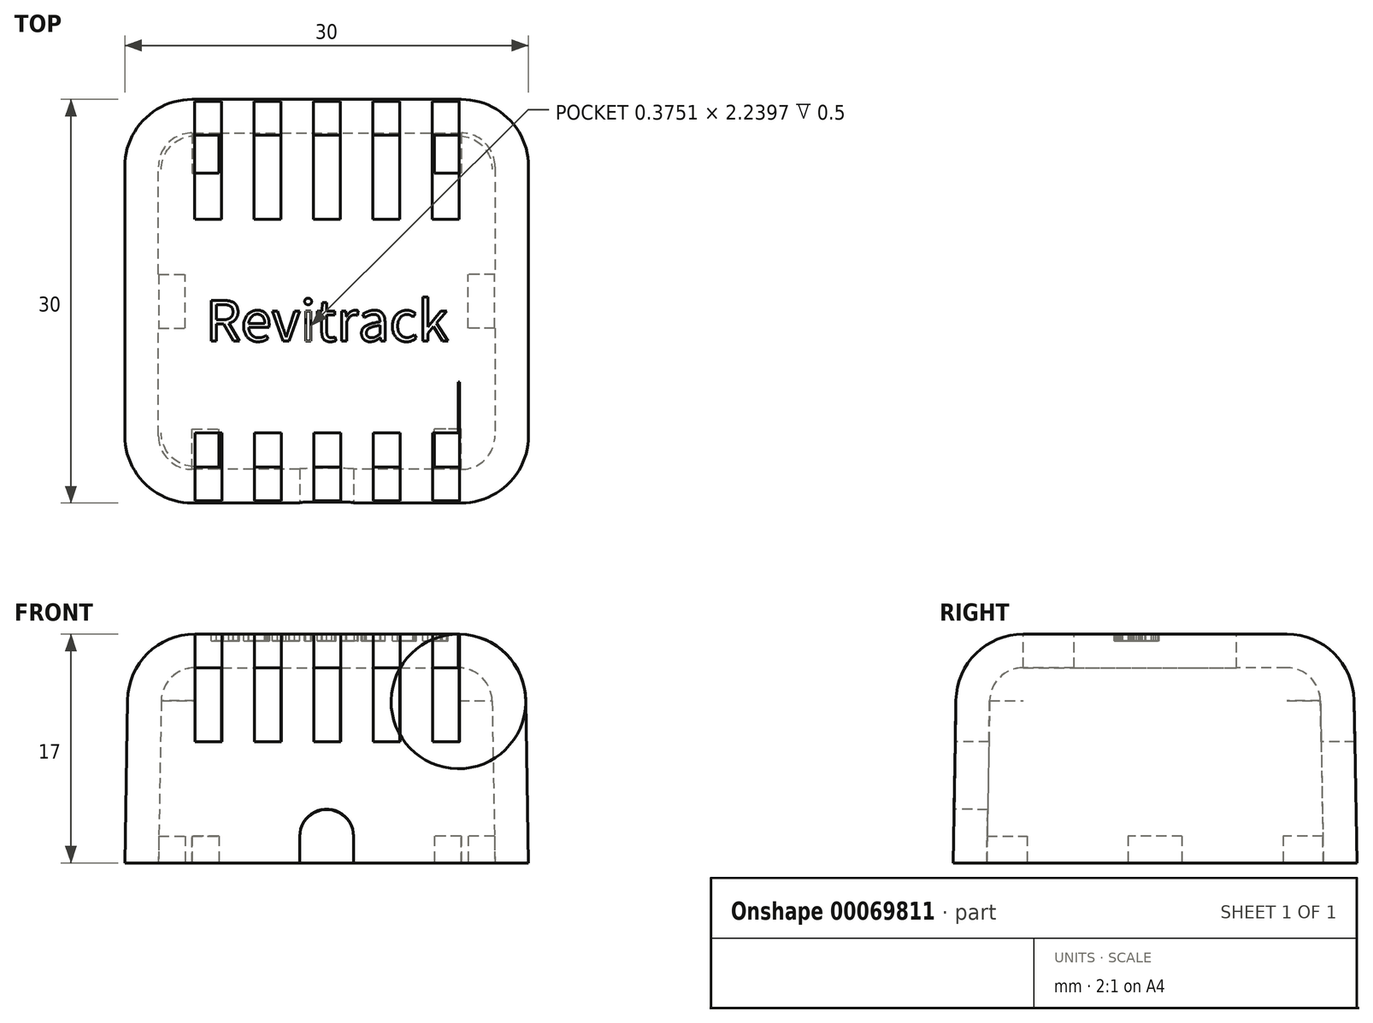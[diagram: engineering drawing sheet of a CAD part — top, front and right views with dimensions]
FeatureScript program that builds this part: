
annotation { "Feature Type Name" : "Feature", "Feature Type Description" : "" }
export const myFeature = defineFeature(function(context is Context, id is Id, definition is map)
    precondition{}
    {
        {
            var Q0;
            Q0=qCreatedBy(makeId("Top.planeOp"),FACE);
            var sketch = newSketch(context, id + "F0", { "sketchPlane" : qUnion([Q0])});
            skLineSegment(sketch, "E0.rect.bottom", {"start": v(15, 15) * mm, "end": v(-15, 15) * mm});
            skLineSegment(sketch, "E0.rect.top", {"start": v(15, -15) * mm, "end": v(-15, -15) * mm});
            skLineSegment(sketch, "E0.rect.left", {"start": v(15, 15) * mm, "end": v(15, -15) * mm});
            skLineSegment(sketch, "E0.rect.right", {"start": v(-15, 15) * mm, "end": v(-15, -15) * mm});
            skPoint(sketch, "E0.rect.middle", {"position": v(0, 0) * mm});
            skSolve(sketch);
        }
        {
            var Q0;
            Q0=makeQuery(id+"F0.imprint","IMPRINT",FACE,{"disambiguationData":[TD([[makeQuery(id+"F0.imprint","IMPRINT",EDGE,{"derivedFrom":sQuery(id+"F0.wireOp",EDGE,"E0.rect.bottom")}),1.0]])]});
            extrude(context, id + "F1", {"entities" : qUnion([Q0]), "depth" : 17 * mm, "hasDraft" : true, "draftAngle" : 1 * degree, "draftPullDirection" : true});
        }
        {
            var Q0;
            Q0=makeQuery(id+"F1.opExtrude","CAP_FACE",FACE,{"disambiguationData":[OSD([sQuery(id+"F0.wireOp",EDGE,"E0.rect.bottom"),sQuery(id+"F0.wireOp",EDGE,"E0.rect.top"),sQuery(id+"F0.wireOp",EDGE,"E0.rect.left"),sQuery(id+"F0.wireOp",EDGE,"E0.rect.right")])],"isStart":false});
            var Q1;
            Q1=makeQuery(id+"F1.opExtrude","SWEPT_EDGE",EDGE,{"disambiguationData":[OSD([sQuery(id+"F0.wireOp",EDGE,"E0.rect.bottom"),sQuery(id+"F0.wireOp",EDGE,"E0.rect.left")])]});
            var Q2;
            Q2=makeQuery(id+"F1.opExtrude","SWEPT_EDGE",EDGE,{"disambiguationData":[OSD([sQuery(id+"F0.wireOp",EDGE,"E0.rect.top"),sQuery(id+"F0.wireOp",EDGE,"E0.rect.left")])]});
            var Q3;
            Q3=makeQuery(id+"F1.opExtrude","SWEPT_EDGE",EDGE,{"disambiguationData":[OSD([sQuery(id+"F0.wireOp",EDGE,"E0.rect.top"),sQuery(id+"F0.wireOp",EDGE,"E0.rect.right")])]});
            var Q4;
            Q4=makeQuery(id+"F1.opExtrude","SWEPT_EDGE",EDGE,{"disambiguationData":[OSD([sQuery(id+"F0.wireOp",EDGE,"E0.rect.bottom"),sQuery(id+"F0.wireOp",EDGE,"E0.rect.right")])]});
            fillet(context, id + "F2", {"entities" : qUnion([Q0, Q1, Q2, Q3, Q4]), "radius" : 5 * mm, "tangentPropagation" : true, "allowEdgeOverflow" : false});
        }
        {
            var Q0;
            Q0=makeQuery(id+"F1.opExtrude","CAP_FACE",FACE,{"disambiguationData":[OSD([sQuery(id+"F0.wireOp",EDGE,"E0.rect.bottom"),sQuery(id+"F0.wireOp",EDGE,"E0.rect.top"),sQuery(id+"F0.wireOp",EDGE,"E0.rect.left"),sQuery(id+"F0.wireOp",EDGE,"E0.rect.right")])],"isStart":true});
            shell(context, id + "F3", {"entities" : qUnion([Q0]), "thickness" : 2.5 * mm});
        }
        {
            var Q0;
            Q0=makeQuery(id+"F1.opExtrude","CAP_FACE",FACE,{"disambiguationData":[OSD([sQuery(id+"F0.wireOp",EDGE,"E0.rect.bottom"),sQuery(id+"F0.wireOp",EDGE,"E0.rect.top"),sQuery(id+"F0.wireOp",EDGE,"E0.rect.left"),sQuery(id+"F0.wireOp",EDGE,"E0.rect.right")])],"isStart":false});
            var sketch = newSketch(context, id + "F4", { "sketchPlane" : qUnion([Q0])});
            skLineSegment(sketch, "E1", {"start": v(0, 9.79) * mm, "end": v(0, -9.79) * mm, "construction": true});
            skLineSegment(sketch, "E2", {"start": v(-9.79, 6) * mm, "end": v(9.79, 6) * mm});
            skLineSegment(sketch, "E3", {"start": v(-9.79, -6) * mm, "end": v(9.79, -6) * mm});
            skLineSegment(sketch, "E4", {"start": v(-9.79, 0) * mm, "end": v(9.79, 0) * mm, "construction": true});
            skLineSegment(sketch, "E5.0", {"start": v(10, -15) * mm, "end": v(-10, -15) * mm, "construction": true});
            skEllipticalArc(sketch, "E5.1", {"construction": true});
            skEllipticalArc(sketch, "E6.0", {"construction": true});
            skLineSegment(sketch, "E7.0", {"start": v(15, 10) * mm, "end": v(15, -10) * mm, "construction": true});
            skEllipticalArc(sketch, "E8.0", {"construction": true});
            skLineSegment(sketch, "E9.0", {"start": v(10, 15) * mm, "end": v(-10, 15) * mm, "construction": true});
            skEllipticalArc(sketch, "E10.0", {"construction": true});
            skLineSegment(sketch, "E11.0", {"start": v(-15, 10) * mm, "end": v(-15, -10) * mm, "construction": true});
            skLineSegment(sketch, "E12.bottom", {"start": v(-9.79, -6) * mm, "end": v(-7.79, -6) * mm});
            skLineSegment(sketch, "E12.top", {"start": v(-9.79, -15) * mm, "end": v(-7.79, -15) * mm});
            skLineSegment(sketch, "E12.left", {"start": v(-9.79, -6) * mm, "end": v(-9.79, -15) * mm});
            skLineSegment(sketch, "E12.right", {"start": v(-7.79, -6) * mm, "end": v(-7.79, -15) * mm});
            skLineSegment(sketch, "E13.0.1.0", {"start": v(-9.8, 15.07) * mm, "end": v(-7.8, 15.07) * mm});
            skLineSegment(sketch, "E13.0.1.1", {"start": v(-9.8, 15.07) * mm, "end": v(-9.8, 6.07) * mm});
            skLineSegment(sketch, "E13.0.1.2", {"start": v(-7.8, 15.07) * mm, "end": v(-7.8, 6.07) * mm});
            skLineSegment(sketch, "E13.0.1.3", {"start": v(-9.8, 6.07) * mm, "end": v(-7.8, 6.07) * mm});
            skLineSegment(sketch, "E13.1.0.0", {"start": v(-5.38, -6) * mm, "end": v(-3.38, -6) * mm});
            skLineSegment(sketch, "E13.1.0.1", {"start": v(-5.38, -6) * mm, "end": v(-5.38, -15) * mm});
            skLineSegment(sketch, "E13.1.0.2", {"start": v(-3.38, -6) * mm, "end": v(-3.38, -15) * mm});
            skLineSegment(sketch, "E13.1.0.3", {"start": v(-5.38, -15) * mm, "end": v(-3.38, -15) * mm});
            skLineSegment(sketch, "E13.1.1.0", {"start": v(-5.39, 15.07) * mm, "end": v(-3.39, 15.07) * mm});
            skLineSegment(sketch, "E13.1.1.1", {"start": v(-5.39, 15.07) * mm, "end": v(-5.39, 6.07) * mm});
            skLineSegment(sketch, "E13.1.1.2", {"start": v(-3.39, 15.07) * mm, "end": v(-3.39, 6.07) * mm});
            skLineSegment(sketch, "E13.1.1.3", {"start": v(-5.39, 6.07) * mm, "end": v(-3.39, 6.07) * mm});
            skLineSegment(sketch, "E13.2.0.0", {"start": v(-0.97, -6) * mm, "end": v(1.03, -6) * mm});
            skLineSegment(sketch, "E13.2.0.1", {"start": v(-0.97, -6) * mm, "end": v(-0.97, -15) * mm});
            skLineSegment(sketch, "E13.2.0.2", {"start": v(1.03, -6) * mm, "end": v(1.03, -15) * mm});
            skLineSegment(sketch, "E13.2.0.3", {"start": v(-0.97, -15) * mm, "end": v(1.03, -15) * mm});
            skLineSegment(sketch, "E13.2.1.0", {"start": v(-0.98, 15.07) * mm, "end": v(1.02, 15.07) * mm});
            skLineSegment(sketch, "E13.2.1.1", {"start": v(-0.98, 15.07) * mm, "end": v(-0.98, 6.07) * mm});
            skLineSegment(sketch, "E13.2.1.2", {"start": v(1.02, 15.07) * mm, "end": v(1.02, 6.07) * mm});
            skLineSegment(sketch, "E13.2.1.3", {"start": v(-0.98, 6.07) * mm, "end": v(1.02, 6.07) * mm});
            skLineSegment(sketch, "E13.direction1", {"start": v(-9.79, -15) * mm, "end": v(-5.38, -15) * mm, "construction": true});
            skLineSegment(sketch, "E13.direction2", {"start": v(-9.79, -15) * mm, "end": v(-9.8, 6.07) * mm, "construction": true});
            skLineSegment(sketch, "E14.0.3.0", {"start": v(3.45, -6) * mm, "end": v(5.45, -6) * mm});
            skLineSegment(sketch, "E14.3.3.0", {"start": v(3.45, -6) * mm, "end": v(3.45, -15) * mm});
            skLineSegment(sketch, "E14.6.3.0", {"start": v(5.45, -6) * mm, "end": v(5.45, -15) * mm});
            skLineSegment(sketch, "E14.9.3.0", {"start": v(3.45, -15) * mm, "end": v(5.45, -15) * mm});
            skLineSegment(sketch, "E14.0.3.1", {"start": v(3.44, 15.07) * mm, "end": v(5.44, 15.07) * mm});
            skLineSegment(sketch, "E14.3.3.1", {"start": v(3.44, 15.07) * mm, "end": v(3.44, 6.07) * mm});
            skLineSegment(sketch, "E14.6.3.1", {"start": v(5.44, 15.07) * mm, "end": v(5.44, 6.07) * mm});
            skLineSegment(sketch, "E14.9.3.1", {"start": v(3.44, 6.07) * mm, "end": v(5.44, 6.07) * mm});
            skLineSegment(sketch, "E14.0.4.0", {"start": v(7.86, -6) * mm, "end": v(9.86, -6) * mm});
            skLineSegment(sketch, "E14.3.4.0", {"start": v(7.86, -6) * mm, "end": v(7.86, -15) * mm});
            skLineSegment(sketch, "E14.6.4.0", {"start": v(9.86, -6) * mm, "end": v(9.86, -15) * mm});
            skLineSegment(sketch, "E14.9.4.0", {"start": v(7.86, -15) * mm, "end": v(9.86, -15) * mm});
            skLineSegment(sketch, "E14.0.4.1", {"start": v(7.85, 15.07) * mm, "end": v(9.85, 15.07) * mm});
            skLineSegment(sketch, "E14.3.4.1", {"start": v(7.85, 15.07) * mm, "end": v(7.85, 6.07) * mm});
            skLineSegment(sketch, "E14.6.4.1", {"start": v(9.85, 15.07) * mm, "end": v(9.85, 6.07) * mm});
            skLineSegment(sketch, "E14.9.4.1", {"start": v(7.85, 6.07) * mm, "end": v(9.85, 6.07) * mm});
            const initialGuessF4  = {"E5.1": [-0.009999238359780454, -0.009999238359780454, -0.7071067811865477, -0.7071067811865474, 0.005001523164455246, 0.005, 5.497939437029719, 0.785245870149869], "E6.0": [0.00999923835978046, -0.009999238359780456, 0.7071067811865475, -0.7071067811865477, 0.005001523164455246, 0.005, 5.497939437029718, 0.7852458701498678], "E8.0": [0.009999238359780466, 0.009999238359780454, 0.7071067811865477, 0.7071067811865474, 0.005001523164455246, 0.005, 5.497939437029719, 0.785245870149869], "E10.0": [-0.009999238359780447, 0.009999238359780453, -0.7071067811865475, 0.7071067811865477, 0.005001523164455246, 0.005, 5.497939437029718, 0.7852458701498678]};
            skSetInitialGuess(sketch, initialGuessF4);
            skSolve(sketch);
        }
        {
            var Q0;
            {var subQ10=sQuery(id+"F4.wireOp",EDGE,"E13.0.1.0");Q0=makeQuery(id+"F4.imprint","IMPRINT",FACE,{"disambiguationData":[TD([[makeQuery(id+"F4.imprint","IMPRINT",EDGE,{"derivedFrom":subQ10}),-1.0]])]});}
            var Q1;
            {var subQ0=sQuery(id+"F4.wireOp",EDGE,"E13.1.1.0");Q1=makeQuery(id+"F4.imprint","IMPRINT",FACE,{"disambiguationData":[TD([[makeQuery(id+"F4.imprint","IMPRINT",EDGE,{"derivedFrom":subQ0}),-1.0]])]});}
            var Q2;
            {var subQ0=sQuery(id+"F4.wireOp",EDGE,"E13.2.1.0");Q2=makeQuery(id+"F4.imprint","IMPRINT",FACE,{"disambiguationData":[TD([[makeQuery(id+"F4.imprint","IMPRINT",EDGE,{"derivedFrom":subQ0}),-1.0]])]});}
            var Q3;
            {var subQ0=sQuery(id+"F4.wireOp",EDGE,"E14.0.3.1");Q3=makeQuery(id+"F4.imprint","IMPRINT",FACE,{"disambiguationData":[TD([[makeQuery(id+"F4.imprint","IMPRINT",EDGE,{"derivedFrom":subQ0}),-1.0]])]});}
            var Q4;
            {var subQ0=sQuery(id+"F4.wireOp",EDGE,"E14.0.4.1");Q4=makeQuery(id+"F4.imprint","IMPRINT",FACE,{"disambiguationData":[TD([[makeQuery(id+"F4.imprint","IMPRINT",EDGE,{"derivedFrom":subQ0}),-1.0]])]});}
            var Q5;
            {var subQ0=sQuery(id+"F4.wireOp",EDGE,"E14.9.4.1");Q5=makeQuery(id+"F4.imprint","IMPRINT",FACE,{"disambiguationData":[TD([[makeQuery(id+"F4.imprint","IMPRINT",EDGE,{"derivedFrom":subQ0}),1.0]])]});}
            var Q6;
            {var subQ0=sQuery(id+"F4.wireOp",EDGE,"E14.9.3.1");Q6=makeQuery(id+"F4.imprint","IMPRINT",FACE,{"disambiguationData":[TD([[makeQuery(id+"F4.imprint","IMPRINT",EDGE,{"derivedFrom":subQ0}),1.0]])]});}
            var Q7;
            {var subQ0=sQuery(id+"F4.wireOp",EDGE,"E13.2.1.3");Q7=makeQuery(id+"F4.imprint","IMPRINT",FACE,{"disambiguationData":[TD([[makeQuery(id+"F4.imprint","IMPRINT",EDGE,{"derivedFrom":subQ0}),1.0]])]});}
            var Q8;
            {var subQ0=sQuery(id+"F4.wireOp",EDGE,"E13.1.1.3");Q8=makeQuery(id+"F4.imprint","IMPRINT",FACE,{"disambiguationData":[TD([[makeQuery(id+"F4.imprint","IMPRINT",EDGE,{"derivedFrom":subQ0}),1.0]])]});}
            var Q9;
            {var subQ0=sQuery(id+"F4.wireOp",EDGE,"E13.0.1.3");var subQ1=sQuery(id+"F4.wireOp",EDGE,"E13.0.1.2");var subQ2=makeQuery(id+"F4.imprint","INTERSECT",VERTEX,{"derivedFrom":[subQ1,subQ0]});Q9=makeQuery(id+"F4.imprint","IMPRINT",FACE,{"disambiguationData":[TD([[makeQuery(id+"F4.imprint","IMPRINT",EDGE,{"disambiguationData":[TD([[subQ2,1.0]])],"derivedFrom":subQ1}),-1.0]])]});}
            var Q10;
            {var subQ0=sQuery(id+"F4.wireOp",EDGE,"E12.bottom");Q10=makeQuery(id+"F4.imprint","IMPRINT",FACE,{"disambiguationData":[TD([[makeQuery(id+"F4.imprint","IMPRINT",EDGE,{"derivedFrom":subQ0}),-1.0]])]});}
            var Q11;
            {var subQ0=sQuery(id+"F4.wireOp",EDGE,"E12.top");Q11=makeQuery(id+"F4.imprint","IMPRINT",FACE,{"disambiguationData":[TD([[makeQuery(id+"F4.imprint","IMPRINT",EDGE,{"derivedFrom":subQ0}),1.0]])]});}
            var Q12;
            {var subQ0=sQuery(id+"F4.wireOp",EDGE,"E13.1.0.0");Q12=makeQuery(id+"F4.imprint","IMPRINT",FACE,{"disambiguationData":[TD([[makeQuery(id+"F4.imprint","IMPRINT",EDGE,{"derivedFrom":subQ0}),-1.0]])]});}
            var Q13;
            {var subQ0=sQuery(id+"F4.wireOp",EDGE,"E13.1.0.3");Q13=makeQuery(id+"F4.imprint","IMPRINT",FACE,{"disambiguationData":[TD([[makeQuery(id+"F4.imprint","IMPRINT",EDGE,{"derivedFrom":subQ0}),1.0]])]});}
            var Q14;
            {var subQ0=sQuery(id+"F4.wireOp",EDGE,"E13.2.0.0");Q14=makeQuery(id+"F4.imprint","IMPRINT",FACE,{"disambiguationData":[TD([[makeQuery(id+"F4.imprint","IMPRINT",EDGE,{"derivedFrom":subQ0}),-1.0]])]});}
            var Q15;
            {var subQ0=sQuery(id+"F4.wireOp",EDGE,"E13.2.0.3");Q15=makeQuery(id+"F4.imprint","IMPRINT",FACE,{"disambiguationData":[TD([[makeQuery(id+"F4.imprint","IMPRINT",EDGE,{"derivedFrom":subQ0}),1.0]])]});}
            var Q16;
            {var subQ0=sQuery(id+"F4.wireOp",EDGE,"E14.0.3.0");Q16=makeQuery(id+"F4.imprint","IMPRINT",FACE,{"disambiguationData":[TD([[makeQuery(id+"F4.imprint","IMPRINT",EDGE,{"derivedFrom":subQ0}),-1.0]])]});}
            var Q17;
            {var subQ0=sQuery(id+"F4.wireOp",EDGE,"E14.9.3.0");Q17=makeQuery(id+"F4.imprint","IMPRINT",FACE,{"disambiguationData":[TD([[makeQuery(id+"F4.imprint","IMPRINT",EDGE,{"derivedFrom":subQ0}),1.0]])]});}
            var Q18;
            {var subQ0=sQuery(id+"F4.wireOp",EDGE,"E14.0.4.0");Q18=makeQuery(id+"F4.imprint","IMPRINT",FACE,{"disambiguationData":[TD([[makeQuery(id+"F4.imprint","IMPRINT",EDGE,{"derivedFrom":subQ0}),-1.0]])]});}
            var Q19;
            {var subQ0=sQuery(id+"F4.wireOp",EDGE,"E14.9.4.0");Q19=makeQuery(id+"F4.imprint","IMPRINT",FACE,{"disambiguationData":[TD([[makeQuery(id+"F4.imprint","IMPRINT",EDGE,{"derivedFrom":subQ0}),1.0]])]});}
            extrude(context, id + "F5", {"entities" : qUnion([Q0, Q1, Q2, Q3, Q4, Q5, Q6, Q7, Q8, Q9, Q10, Q11, Q12, Q13, Q14, Q15, Q16, Q17, Q18, Q19]), "operationType" : NewBodyOperationType.REMOVE, "oppositeDirection" : true, "depth" : 8 * mm});
        }
        {
            var Q0;
            Q0=makeQuery(id+"F1.opExtrude","SWEPT_FACE",FACE,{"disambiguationData":[OSD([sQuery(id+"F0.wireOp",EDGE,"E0.rect.top")])]});
            var sketch = newSketch(context, id + "F6", { "sketchPlane" : qUnion([Q0])});
            skCircle(sketch, "E15", {"center": v(0, 1.74) * mm, "radius": 2 * mm});
            skLineSegment(sketch, "E16", {"start": v(-2, 1.74) * mm, "end": v(-2, -0.26) * mm});
            skLineSegment(sketch, "E17", {"start": v(2, 1.74) * mm, "end": v(2, -0.26) * mm});
            skSolve(sketch);
        }
        {
            var Q0;
            {var subQ0=sQuery(id+"F6.wireOp",EDGE,"E16");Q0=makeQuery(id+"F6.imprint","IMPRINT",FACE,{"disambiguationData":[TD([[makeQuery(id+"F6.imprint","IMPRINT",EDGE,{"derivedFrom":subQ0}),1.0]])]});}
            var Q1;
            {var subQ0=sQuery(id+"F6.wireOp",EDGE,"E15");var subQ1=makeQuery(id+"F6.imprint","INTERSECT",VERTEX,{"derivedFrom":[subQ0,sQuery(id+"F6.wireOp",EDGE,"E16")]});Q1=makeQuery(id+"F6.imprint","IMPRINT",FACE,{"disambiguationData":[TD([[makeQuery(id+"F6.imprint","IMPRINT",EDGE,{"disambiguationData":[TD([[subQ1,1.0]])],"derivedFrom":subQ0}),1.0]])]});}
            var Q2;
            {var subQ0=sQuery(id+"F6.wireOp",EDGE,"E17");Q2=makeQuery(id+"F6.imprint","IMPRINT",FACE,{"disambiguationData":[TD([[makeQuery(id+"F6.imprint","IMPRINT",EDGE,{"derivedFrom":subQ0}),-1.0]])]});}
            extrude(context, id + "F7", {"entities" : qUnion([Q0, Q1, Q2]), "operationType" : NewBodyOperationType.REMOVE, "oppositeDirection" : true, "depth" : 25 * mm});
        }
        {
            var Q0;
            Q0=makeQuery(id+"F1.opExtrude","CAP_FACE",FACE,{"disambiguationData":[OSD([sQuery(id+"F0.wireOp",EDGE,"E0.rect.bottom"),sQuery(id+"F0.wireOp",EDGE,"E0.rect.top"),sQuery(id+"F0.wireOp",EDGE,"E0.rect.left"),sQuery(id+"F0.wireOp",EDGE,"E0.rect.right")])],"isStart":false});
            var sketch = newSketch(context, id + "F8", { "sketchPlane" : qUnion([Q0])});
            skText(sketch, "E18", { "text": "Revitrack", "fontName": "NotoSansCJKtc-Regular.otf"});
            const initialGuessF8  = {"E18": [-0.009, -0.00297, 1, 0, 0.00297]};
            skSetInitialGuess(sketch, initialGuessF8);
            skSolve(sketch);
        }
        {
            var Q0;
            Q0=makeQuery(id+"F8.imprint","IMPRINT",FACE,{"disambiguationData":[TD([[makeQuery(id+"F8.imprint","IMPRINT",EDGE,{"derivedFrom":sQuery(id+"F8.wireOp",EDGE,"E18.sketch_text.stroke-0")}),1.0]])]});
            var Q1;
            Q1=makeQuery(id+"F8.imprint","IMPRINT",FACE,{"disambiguationData":[TD([[makeQuery(id+"F8.imprint","IMPRINT",EDGE,{"derivedFrom":sQuery(id+"F8.wireOp",EDGE,"E18.sketch_text.stroke-15")}),1.0]])]});
            var Q2;
            Q2=makeQuery(id+"F8.imprint","IMPRINT",FACE,{"disambiguationData":[TD([[makeQuery(id+"F8.imprint","IMPRINT",EDGE,{"derivedFrom":sQuery(id+"F8.wireOp",EDGE,"E18.sketch_text.stroke-27")}),1.0]])]});
            var Q3;
            Q3=makeQuery(id+"F8.imprint","IMPRINT",FACE,{"disambiguationData":[TD([[makeQuery(id+"F8.imprint","IMPRINT",EDGE,{"derivedFrom":sQuery(id+"F8.wireOp",EDGE,"E18.sketch_text.stroke-37")}),1.0]])]});
            var Q4;
            Q4=makeQuery(id+"F8.imprint","IMPRINT",FACE,{"disambiguationData":[TD([[makeQuery(id+"F8.imprint","IMPRINT",EDGE,{"derivedFrom":sQuery(id+"F8.wireOp",EDGE,"E18.sketch_text.stroke-41")}),1.0]])]});
            var Q5;
            Q5=makeQuery(id+"F8.imprint","IMPRINT",FACE,{"disambiguationData":[TD([[makeQuery(id+"F8.imprint","IMPRINT",EDGE,{"derivedFrom":sQuery(id+"F8.wireOp",EDGE,"E18.sketch_text.stroke-45")}),1.0]])]});
            var Q6;
            Q6=makeQuery(id+"F8.imprint","IMPRINT",FACE,{"disambiguationData":[TD([[makeQuery(id+"F8.imprint","IMPRINT",EDGE,{"derivedFrom":sQuery(id+"F8.wireOp",EDGE,"E18.sketch_text.stroke-61")}),1.0]])]});
            var Q7;
            Q7=makeQuery(id+"F8.imprint","IMPRINT",FACE,{"disambiguationData":[TD([[makeQuery(id+"F8.imprint","IMPRINT",EDGE,{"derivedFrom":sQuery(id+"F8.wireOp",EDGE,"E18.sketch_text.stroke-72")}),1.0]])]});
            var Q8;
            Q8=makeQuery(id+"F8.imprint","IMPRINT",FACE,{"disambiguationData":[TD([[makeQuery(id+"F8.imprint","IMPRINT",EDGE,{"derivedFrom":sQuery(id+"F8.wireOp",EDGE,"E18.sketch_text.stroke-88")}),1.0]])]});
            var Q9;
            Q9=makeQuery(id+"F8.imprint","IMPRINT",FACE,{"disambiguationData":[TD([[makeQuery(id+"F8.imprint","IMPRINT",EDGE,{"derivedFrom":sQuery(id+"F8.wireOp",EDGE,"E18.sketch_text.stroke-98")}),1.0]])]});
            extrude(context, id + "F9", {"entities" : qUnion([Q0, Q1, Q2, Q3, Q4, Q5, Q6, Q7, Q8, Q9]), "operationType" : NewBodyOperationType.REMOVE, "oppositeDirection" : true, "depth" : 0.5 * mm});
        }
        {
            var Q0;
            Q0=makeQuery(id+"F1.opExtrude","CAP_FACE",FACE,{"disambiguationData":[OSD([sQuery(id+"F0.wireOp",EDGE,"E0.rect.bottom"),sQuery(id+"F0.wireOp",EDGE,"E0.rect.top"),sQuery(id+"F0.wireOp",EDGE,"E0.rect.left"),sQuery(id+"F0.wireOp",EDGE,"E0.rect.right")])],"isStart":true});
            var sketch = newSketch(context, id + "F10", { "sketchPlane" : qUnion([Q0])});
            skLineSegment(sketch, "E19", {"start": v(0, 21.6) * mm, "end": v(0, -21.15) * mm, "construction": true});
            skLineSegment(sketch, "E20.bottom", {"start": v(-10, 12.5) * mm, "end": v(-8, 12.5) * mm});
            skLineSegment(sketch, "E20.top", {"start": v(-10, 9.5) * mm, "end": v(-8, 9.5) * mm});
            skLineSegment(sketch, "E20.left", {"start": v(-10, 12.5) * mm, "end": v(-10, 9.5) * mm});
            skLineSegment(sketch, "E20.right", {"start": v(-8, 12.5) * mm, "end": v(-8, 9.5) * mm});
            skLineSegment(sketch, "E21.bottom", {"start": v(-10, -12.5) * mm, "end": v(-8, -12.5) * mm});
            skLineSegment(sketch, "E21.top", {"start": v(-10, -9.5) * mm, "end": v(-8, -9.5) * mm});
            skLineSegment(sketch, "E21.left", {"start": v(-10, -12.5) * mm, "end": v(-10, -9.5) * mm});
            skLineSegment(sketch, "E21.right", {"start": v(-8, -12.5) * mm, "end": v(-8, -9.5) * mm});
            skLineSegment(sketch, "E22.MirrorCS", {"start": v(8, 12.5) * mm, "end": v(8, 9.5) * mm});
            skLineSegment(sketch, "E23.MirrorCS", {"start": v(10, 9.5) * mm, "end": v(8, 9.5) * mm});
            skLineSegment(sketch, "E24.MirrorCS", {"start": v(10, 12.5) * mm, "end": v(8, 12.5) * mm});
            skLineSegment(sketch, "E25.MirrorCS", {"start": v(10, 12.5) * mm, "end": v(10, 9.5) * mm});
            skLineSegment(sketch, "E26.MirrorCS", {"start": v(10, -12.5) * mm, "end": v(10, -9.5) * mm});
            skLineSegment(sketch, "E27.MirrorCS", {"start": v(8, -12.5) * mm, "end": v(8, -9.5) * mm});
            skLineSegment(sketch, "E28.MirrorCS", {"start": v(10, -12.5) * mm, "end": v(8, -12.5) * mm});
            skLineSegment(sketch, "E29.MirrorCS", {"start": v(10, -9.5) * mm, "end": v(8, -9.5) * mm});
            skLineSegment(sketch, "E30.bottom", {"start": v(-12.5, 2) * mm, "end": v(-10.5, 2) * mm});
            skLineSegment(sketch, "E30.top", {"start": v(-12.5, -2) * mm, "end": v(-10.5, -2) * mm});
            skLineSegment(sketch, "E30.left", {"start": v(-12.5, 2) * mm, "end": v(-12.5, -2) * mm});
            skLineSegment(sketch, "E30.right", {"start": v(-10.5, 2) * mm, "end": v(-10.5, -2) * mm});
            skLineSegment(sketch, "E31.MirrorCS", {"start": v(10.5, 2) * mm, "end": v(10.5, -2) * mm});
            skLineSegment(sketch, "E32.MirrorCS", {"start": v(12.5, 2) * mm, "end": v(10.5, 2) * mm});
            skLineSegment(sketch, "E33.MirrorCS", {"start": v(12.5, -2) * mm, "end": v(10.5, -2) * mm});
            skLineSegment(sketch, "E34.MirrorCS", {"start": v(12.5, 2) * mm, "end": v(12.5, -2) * mm});
            skLineSegment(sketch, "E35", {"start": v(-8, 12.5) * mm, "end": v(-8, -12.5) * mm, "construction": true});
            skLineSegment(sketch, "E36", {"start": v(-10, 12.5) * mm, "end": v(-10, -12.5) * mm, "construction": true});
            skSolve(sketch);
        }
        {
            var Q0;
            Q0=makeQuery(id+"F10.imprint","IMPRINT",FACE,{"disambiguationData":[TD([[makeQuery(id+"F10.imprint","IMPRINT",EDGE,{"derivedFrom":sQuery(id+"F10.wireOp",EDGE,"E30.bottom")}),-1.0]])]});
            var Q1;
            Q1=makeQuery(id+"F10.imprint","IMPRINT",FACE,{"disambiguationData":[TD([[makeQuery(id+"F10.imprint","IMPRINT",EDGE,{"derivedFrom":sQuery(id+"F10.wireOp",EDGE,"E20.bottom")}),1.0]])]});
            var Q2;
            Q2=makeQuery(id+"F10.imprint","IMPRINT",FACE,{"disambiguationData":[TD([[makeQuery(id+"F10.imprint","IMPRINT",EDGE,{"derivedFrom":sQuery(id+"F10.wireOp",EDGE,"E22.MirrorCS")}),1.0]])]});
            var Q3;
            Q3=makeQuery(id+"F10.imprint","IMPRINT",FACE,{"disambiguationData":[TD([[makeQuery(id+"F10.imprint","IMPRINT",EDGE,{"derivedFrom":sQuery(id+"F10.wireOp",EDGE,"E31.MirrorCS")}),1.0]])]});
            var Q4;
            Q4=makeQuery(id+"F10.imprint","IMPRINT",FACE,{"disambiguationData":[TD([[makeQuery(id+"F10.imprint","IMPRINT",EDGE,{"derivedFrom":sQuery(id+"F10.wireOp",EDGE,"E26.MirrorCS")}),1.0]])]});
            var Q5;
            Q5=makeQuery(id+"F10.imprint","IMPRINT",FACE,{"disambiguationData":[TD([[makeQuery(id+"F10.imprint","IMPRINT",EDGE,{"derivedFrom":sQuery(id+"F10.wireOp",EDGE,"E21.bottom")}),-1.0]])]});
            extrude(context, id + "F11", {"entities" : qUnion([Q0, Q1, Q2, Q3, Q4, Q5]), "operationType" : NewBodyOperationType.ADD, "oppositeDirection" : true, "depth" : 2 * mm});
        }
    });
